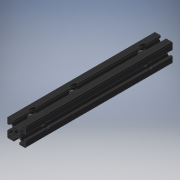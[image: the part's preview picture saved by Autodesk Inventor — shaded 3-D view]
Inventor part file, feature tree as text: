
AUTODESK INVENTOR PART (.ipt)
format: ipt  version: 2019 (Build 230136000, 136)  size: 358,400 bytes
history: native  units: mm
features: other x7, sketch x7, revolve x5, extrude x1, hole x1
ambient origin geometry x8: Origin, YZ Plane, XZ Plane, XY Plane, X Axis, Y Axis, Z Axis, Center Point
bodies: Solid1 (feature_tree)
feature tree (21):
  extrude  "Extrusion1"  TaperAngle=360.0deg  [1 undecoded]
  hole  "Hole1"  [1 undecoded]
  revolve  "Revolution1"  Angle=360.0deg
  revolve  "Revolution2"  [1 undecoded]
  revolve  "Revolution3"  [1 undecoded]
  revolve  "Revolution4"  [1 undecoded]
  revolve  "Revolution5"  [1 undecoded]
  other  "C1_XY"
  other  "C1_YZ"
  other  "C1_ZX"
  other  "C1_X"
  other  "C1_Y"
  other  "C1_Z"
  other  "C1_Center"
  sketch  "Sketch_1"  dims[d0=160.0mm d1=0.0mm]
  sketch  "Sketch2"  dims[d2=4.2mm d3=6.0mm d4=4.0mm d5=2.0mm d6=90.0deg d7=160.0mm d8=0.0mm d9=360.0deg]
  sketch  "Sketch_62"
  sketch  "Sketch_25"  dims[d10=360.0deg d11=360.0deg]
  sketch  "Sketch_30"  dims[d12=360.0deg d13=360.0deg]
  sketch  "Sketch_31"  dims[d14=0.0mm]
  sketch  "Sketch_47"
note: 6 required parameter values undecoded (feature->parameter linkage not recoverable at this tier; creation-order binding heuristic only, values carry confidence <= 0.55)
